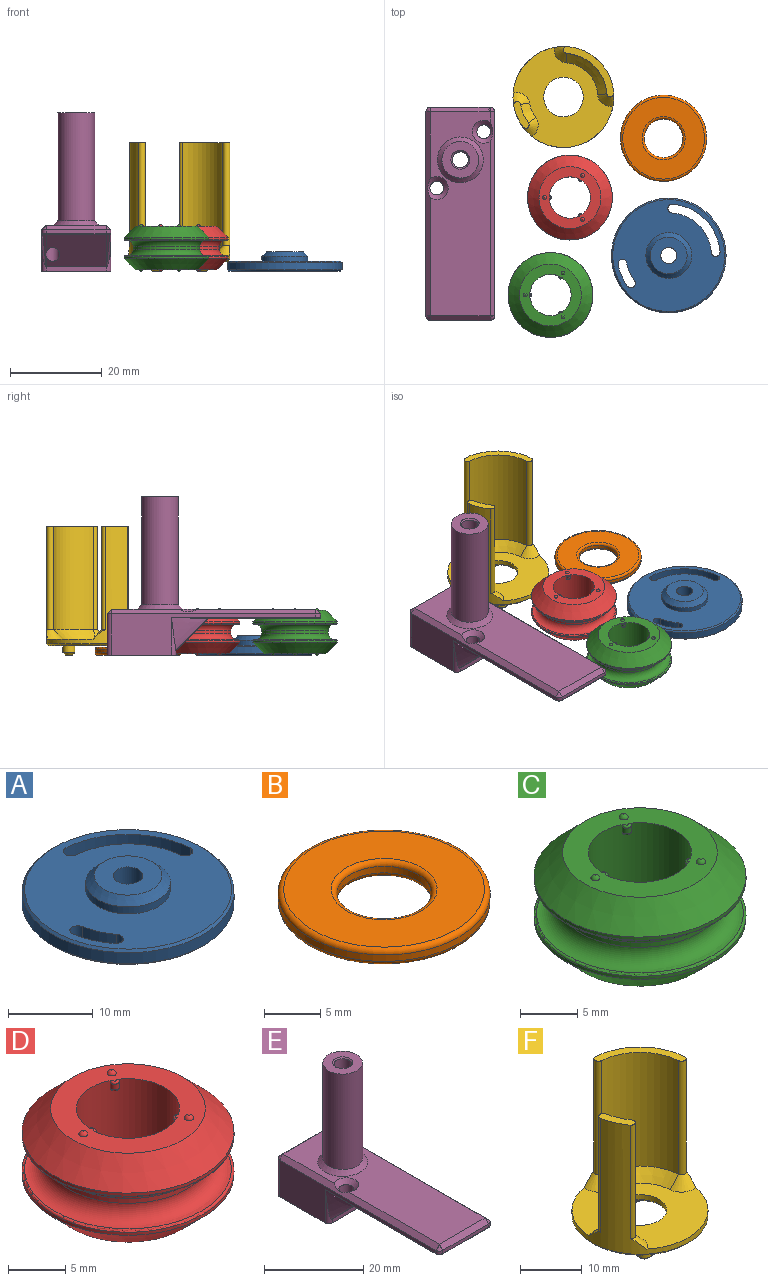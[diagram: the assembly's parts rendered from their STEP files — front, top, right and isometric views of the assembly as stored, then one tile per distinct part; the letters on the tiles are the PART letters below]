
ASSEMBLY  parts=6 mates=5
PART A: 28 faces, bbox 25x25x4.2 mm
  f0: cylinder r=1.75mm len=3.5mm, axis (0,0,1), area 38.5mm2, adj f22,f25
  f1: cylinder r=11.2mm len=4.76mm, axis (0,0,1), area 9.9mm2, adj f2,f7,f11,f16
  f2: cylinder r=0.95mm len=1.9mm, axis (0,0,1), area 5.7mm2, adj f1,f3,f11,f18
  f3: cylinder r=9.3mm len=3.95mm, axis (0,0,1), area 8.2mm2, adj f2,f7,f11,f19
  f4: cylinder r=9.3mm len=8.59mm, axis (0,0,1), area 25.2mm2, adj f5,f8,f11,f12
  f5: cylinder r=0.95mm len=1.9mm, axis (0,0,1), area 5.7mm2, adj f4,f6,f11,f14
  f6: cylinder r=11.2mm len=10.35mm, axis (0,0,1), area 30.3mm2, adj f5,f8,f11,f15
  f7: cylinder r=0.95mm len=1.9mm, axis (0,0,1), area 5.7mm2, adj f1,f3,f11,f17
  f8: cylinder r=0.95mm len=1.9mm, axis (0,0,1), area 5.7mm2, adj f4,f6,f11,f13
  f9: cylinder r=12.5mm len=25mm, axis (0,0,1), area 125.7mm2, adj f20,f21
  f10: plane 24.4x24.4mm, normal (0,0,-1), area 342.8mm2, adj f12,f13,f14,f15,f16,f17,f18,f19
  f11: plane 24.4x24.4mm, normal (0,0,1), area 346.6mm2, adj f1,f2,f3,f4,f5,f6,f7,f8
  f12: cone r=9mm half-angle=45deg, axis (0,0,1), area 5.5mm2, adj f4,f10,f13,f14
  f13: cone r=1.25mm half-angle=45deg, axis (0,0,-1), area 1.5mm2, adj f8,f10,f12,f15
  f14: cone r=1.25mm half-angle=45deg, axis (0,0,-1), area 1.5mm2, adj f5,f10,f12,f15
  f15: cone r=11.5mm half-angle=45deg, axis (0,0,-1), area 6.9mm2, adj f6,f10,f13,f14
  f16: cone r=11.5mm half-angle=45deg, axis (0,0,-1), area 2.2mm2, adj f1,f10,f17,f18
  f17: cone r=1.25mm half-angle=45deg, axis (0,0,-1), area 1.5mm2, adj f7,f10,f16,f19
  f18: cone r=1.25mm half-angle=45deg, axis (0,0,-1), area 1.5mm2, adj f2,f10,f16,f19
  f19: cone r=9mm half-angle=45deg, axis (0,0,1), area 1.8mm2, adj f3,f10,f17,f18
  f20: cone r=12.2mm half-angle=45deg, axis (0,0,-1), area 32.9mm2, adj f9,f11
  f21: cone r=12.5mm half-angle=45deg, axis (0,0,1), area 32.9mm2, adj f9,f10
  f22: plane 8.2x8.2mm, normal (0,0,-1), area 43.2mm2, adj f0,f23
  f23: cylinder r=4.1mm len=8.2mm, axis (0,0,-1), area 5.2mm2, adj f22,f27
  f24: cylinder r=5mm len=10mm, axis (0,0,-1), area 31.4mm2, adj f11,f26
  f25: plane 8x8mm, normal (0,0,1), area 40.6mm2, adj f0,f26
  f26: cone r=4mm half-angle=45deg, axis (0,0,-1), area 40mm2, adj f24,f25
  f27: cone r=4.1mm half-angle=45deg, axis (0,0,-1), area 19.3mm2, adj f10,f23
PART B: 8 faces, bbox 20.3x20.3x1.7 mm
  f0: cylinder r=4.2mm len=8.4mm, axis (0,0,-1), area 18.5mm2, adj f4,f6
  f1: cylinder r=9.4mm len=18.8mm, axis (0,0,-1), area 41.3mm2, adj f5,f7
  f2: plane 17.8x17.8mm, normal (0,0,1), area 179.4mm2, adj f6,f7
  f3: plane 17.8x17.8mm, normal (0,0,-1), area 179.4mm2, adj f4,f5
  f4: torus R=4.7mm, axis (0,0,1), area 21.6mm2, adj f0,f3
  f5: torus R=8.9mm, axis (0,0,1), area 45.5mm2, adj f1,f3
  f6: torus R=4.7mm, axis (0,0,1), area 21.6mm2, adj f0,f2
  f7: torus R=8.9mm, axis (0,0,1), area 45.5mm2, adj f1,f2
PART C: 48 faces, bbox 21.2x21.2x10.1 mm
  f0: cylinder r=4.5mm len=9.5mm, axis (0,0,-1), area 264mm2, adj f2,f6,f8,f9,f10,f11,f12,f13
  f1: cylinder r=9.25mm len=18.5mm, axis (0,0,-1), area 19mm2, adj f3,f46
  f2: plane 13.5x13.5mm, normal (0,0,-1), area 78.2mm2, adj f0,f3,f26,f28,f30,f39,f41,f43
  f3: cone r=8.75mm half-angle=45deg, axis (0,0,1), area 177.7mm2, adj f1,f2
  f4: cylinder r=7.25mm len=14.5mm, axis (0,0,-1), area 22.8mm2, adj f44,f45
  f5: cylinder r=9.25mm len=18.5mm, axis (0,0,-1), area 19mm2, adj f7,f47
  f6: plane 13.5x13.5mm, normal (0,0,1), area 78.2mm2, adj f0,f7,f14,f16,f18,f33,f35,f37
  f7: cone r=6.75mm half-angle=45deg, axis (0,0,-1), area 177.7mm2, adj f5,f6
  f8: plane 0.4x0.2mm, normal (0,0,-1), area 0.1mm2, adj f0,f19
  f9: cylinder r=0.4mm len=0.8mm, axis (0,0,1), area 0.7mm2, adj f0,f18,f19
  f10: plane 0.37x0.3mm, normal (0,0,-1), area 0.1mm2, adj f0,f17
  f11: cylinder r=0.4mm len=0.74mm, axis (0,0,1), area 0.7mm2, adj f0,f16,f17
  f12: plane 0.37x0.3mm, normal (0,0,-1), area 0.1mm2, adj f0,f15
  f13: cylinder r=0.4mm len=0.74mm, axis (0,0,1), area 0.7mm2, adj f0,f14,f15
  f14: torus R=0.2mm, axis (0,0,1), area 0.3mm2, adj f0,f6,f13
  f15: torus R=0.2mm, axis (0,0,1), area 0.3mm2, adj f0,f12,f13
  f16: torus R=0.2mm, axis (0,0,1), area 0.3mm2, adj f0,f6,f11
  f17: torus R=0.2mm, axis (0,0,1), area 0.3mm2, adj f0,f10,f11
  f18: torus R=0.2mm, axis (0,0,1), area 0.3mm2, adj f0,f6,f9
  f19: torus R=0.2mm, axis (0,0,1), area 0.3mm2, adj f0,f8,f9
  f20: plane 0.4x0.2mm, normal (0,0,1), area 0.1mm2, adj f0,f31
  f21: cylinder r=0.4mm len=0.8mm, axis (0,0,-1), area 0.7mm2, adj f0,f30,f31
  f22: plane 0.37x0.3mm, normal (0,0,1), area 0.1mm2, adj f0,f29
  f23: cylinder r=0.4mm len=0.74mm, axis (0,0,-1), area 0.7mm2, adj f0,f28,f29
  f24: plane 0.37x0.3mm, normal (0,0,1), area 0.1mm2, adj f0,f27
  f25: cylinder r=0.4mm len=0.74mm, axis (0,0,-1), area 0.7mm2, adj f0,f26,f27
  f26: torus R=0.2mm, axis (0,0,1), area 0.3mm2, adj f0,f2,f25
  f27: torus R=0.2mm, axis (0,0,-1), area 0.3mm2, adj f0,f24,f25
  f28: torus R=0.2mm, axis (0,0,1), area 0.3mm2, adj f0,f2,f23
  f29: torus R=0.2mm, axis (0,0,-1), area 0.3mm2, adj f0,f22,f23
  f30: torus R=0.2mm, axis (0,0,1), area 0.3mm2, adj f0,f2,f21
  f31: torus R=0.2mm, axis (0,0,-1), area 0.3mm2, adj f0,f20,f21
  f32: plane 0.03x0.03mm, normal (0,0,1), area 0mm2, adj f33
  f33: torus R=0.01mm, axis (0,0,-1), area 0.8mm2, adj f6,f32
  f34: plane 0.03x0.03mm, normal (0,0,1), area 0mm2, adj f35
  f35: torus R=0.01mm, axis (0,0,-1), area 0.8mm2, adj f6,f34
  f36: plane 0.03x0.03mm, normal (0,0,1), area 0mm2, adj f37
  f37: torus R=0.01mm, axis (0,0,-1), area 0.8mm2, adj f6,f36
  f38: plane 0.03x0.03mm, normal (0,0,-1), area 0mm2, adj f39
  f39: torus R=0.01mm, axis (0,0,1), area 0.8mm2, adj f2,f38
  f40: plane 0.03x0.03mm, normal (0,0,-1), area 0mm2, adj f41
  f41: torus R=0.01mm, axis (0,0,1), area 0.8mm2, adj f2,f40
  f42: plane 0.03x0.03mm, normal (0,0,-1), area 0mm2, adj f43
  f43: torus R=0.01mm, axis (0,0,1), area 0.8mm2, adj f2,f42
  f44: torus R=8.75mm, axis (0,0,1), area 130.3mm2, adj f4,f46
  f45: torus R=8.75mm, axis (0,0,1), area 130.3mm2, adj f4,f47
  f46: torus R=9.05mm, axis (0,0,-1), area 20.1mm2, adj f1,f44
  f47: torus R=9.05mm, axis (0,0,-1), area 20.1mm2, adj f5,f45
PART D: 48 faces, bbox 21.2x21.2x10.1 mm
  f0: cylinder r=4.5mm len=9.5mm, axis (0,0,-1), area 264mm2, adj f2,f6,f8,f9,f10,f11,f12,f13
  f1: cylinder r=9.25mm len=18.5mm, axis (0,0,-1), area 19mm2, adj f3,f47
  f2: plane 13.5x13.5mm, normal (0,0,-1), area 78.2mm2, adj f0,f3,f26,f28,f30,f39,f41,f43
  f3: cone r=8.75mm half-angle=45deg, axis (0,0,1), area 177.7mm2, adj f1,f2
  f4: cylinder r=7.25mm len=14.5mm, axis (0,0,-1), area 22.8mm2, adj f44,f45
  f5: cylinder r=9.25mm len=18.5mm, axis (0,0,-1), area 19mm2, adj f7,f46
  f6: plane 13.5x13.5mm, normal (0,0,1), area 78.2mm2, adj f0,f7,f14,f16,f18,f33,f35,f37
  f7: cone r=6.75mm half-angle=45deg, axis (0,0,-1), area 177.7mm2, adj f5,f6
  f8: plane 0.4x0.2mm, normal (0,0,-1), area 0.1mm2, adj f0,f19
  f9: cylinder r=0.4mm len=0.8mm, axis (0,0,1), area 0.7mm2, adj f0,f18,f19
  f10: plane 0.37x0.3mm, normal (0,0,-1), area 0.1mm2, adj f0,f17
  f11: cylinder r=0.4mm len=0.74mm, axis (0,0,1), area 0.7mm2, adj f0,f16,f17
  f12: plane 0.37x0.3mm, normal (0,0,-1), area 0.1mm2, adj f0,f15
  f13: cylinder r=0.4mm len=0.74mm, axis (0,0,1), area 0.7mm2, adj f0,f14,f15
  f14: torus R=0.2mm, axis (0,0,1), area 0.3mm2, adj f0,f6,f13
  f15: torus R=0.2mm, axis (0,0,1), area 0.3mm2, adj f0,f12,f13
  f16: torus R=0.2mm, axis (0,0,1), area 0.3mm2, adj f0,f6,f11
  f17: torus R=0.2mm, axis (0,0,1), area 0.3mm2, adj f0,f10,f11
  f18: torus R=0.2mm, axis (0,0,1), area 0.3mm2, adj f0,f6,f9
  f19: torus R=0.2mm, axis (0,0,1), area 0.3mm2, adj f0,f8,f9
  f20: plane 0.4x0.2mm, normal (0,0,1), area 0.1mm2, adj f0,f31
  f21: cylinder r=0.4mm len=0.8mm, axis (0,0,-1), area 0.7mm2, adj f0,f30,f31
  f22: plane 0.37x0.3mm, normal (0,0,1), area 0.1mm2, adj f0,f29
  f23: cylinder r=0.4mm len=0.74mm, axis (0,0,-1), area 0.7mm2, adj f0,f28,f29
  f24: plane 0.37x0.3mm, normal (0,0,1), area 0.1mm2, adj f0,f27
  f25: cylinder r=0.4mm len=0.74mm, axis (0,0,-1), area 0.7mm2, adj f0,f26,f27
  f26: torus R=0.2mm, axis (0,0,1), area 0.3mm2, adj f0,f2,f25
  f27: torus R=0.2mm, axis (0,0,-1), area 0.3mm2, adj f0,f24,f25
  f28: torus R=0.2mm, axis (0,0,1), area 0.3mm2, adj f0,f2,f23
  f29: torus R=0.2mm, axis (0,0,-1), area 0.3mm2, adj f0,f22,f23
  f30: torus R=0.2mm, axis (0,0,1), area 0.3mm2, adj f0,f2,f21
  f31: torus R=0.2mm, axis (0,0,-1), area 0.3mm2, adj f0,f20,f21
  f32: plane 0.03x0.03mm, normal (0,0,1), area 0mm2, adj f33
  f33: torus R=0.01mm, axis (0,0,-1), area 0.8mm2, adj f6,f32
  f34: plane 0.03x0.03mm, normal (0,0,1), area 0mm2, adj f35
  f35: torus R=0.01mm, axis (0,0,-1), area 0.8mm2, adj f6,f34
  f36: plane 0.03x0.03mm, normal (0,0,1), area 0mm2, adj f37
  f37: torus R=0.01mm, axis (0,0,-1), area 0.8mm2, adj f6,f36
  f38: plane 0.03x0.03mm, normal (0,0,-1), area 0mm2, adj f39
  f39: torus R=0.01mm, axis (0,0,1), area 0.8mm2, adj f2,f38
  f40: plane 0.03x0.03mm, normal (0,0,-1), area 0mm2, adj f41
  f41: torus R=0.01mm, axis (0,0,1), area 0.8mm2, adj f2,f40
  f42: plane 0.03x0.03mm, normal (0,0,-1), area 0mm2, adj f43
  f43: torus R=0.01mm, axis (0,0,1), area 0.8mm2, adj f2,f42
  f44: torus R=8.75mm, axis (0,0,1), area 130.3mm2, adj f4,f47
  f45: torus R=8.75mm, axis (0,0,1), area 130.3mm2, adj f4,f46
  f46: torus R=9.05mm, axis (0,0,-1), area 20.1mm2, adj f5,f45
  f47: torus R=9.05mm, axis (0,0,-1), area 20.1mm2, adj f1,f44
PART E: 41 faces, bbox 16x47.3x35.3 mm
  f0: plane 13x0.8mm, normal (0,-1,0), area 10.4mm2, adj f16,f19,f28,f33
  f1: plane 44.5x9mm, normal (1,0,0), area 142.2mm2, adj f5,f14,f16,f17,f23,f31
  f2: plane 13x9mm, normal (0,1,0), area 117mm2, adj f5,f17,f18,f22
  f3: plane 44.5x9mm, normal (-1,0,0), area 142.2mm2, adj f5,f15,f18,f19,f27,f35
  f4: plane 44.5x13mm, normal (0,0,1), area 467.3mm2, adj f20,f22,f23,f25,f27,f28,f30
  f5: plane 15x15mm, normal (0,0,-1), area 207.5mm2, adj f1,f2,f3,f6,f7,f12,f14,f15
  f6: cylinder r=1.75mm len=34.2mm, axis (0,0,1), area 376mm2, adj f5,f13
  f7: plane 13x1mm, normal (0,-1,0), area 13mm2, adj f5,f14,f15,f38
  f8: plane 24.34x14.6mm, normal (0,0,-1), area 354.5mm2, adj f31,f32,f33,f34,f35,f37,f38,f39
  f9: cylinder r=4mm len=23.5mm, axis (0,0,-1), area 590.6mm2, adj f10,f30
  f10: plane 8x8mm, normal (0,0,1), area 37.1mm2, adj f9,f13
  f11: cylinder r=1.5mm len=6.86mm, axis (0,0,1), area 50.5mm2, adj f25,f37,f38
  f12: cylinder r=1.5mm len=9mm, axis (0,0,1), area 84.8mm2, adj f5,f20
  f13: cone r=1.75mm half-angle=45deg, axis (0,0,1), area 5.1mm2, adj f6,f10
  f14: cylinder r=1mm len=8.2mm, axis (0,0,1), area 5.5mm2, adj f1,f5,f7,f39,f40
  f15: cylinder r=1mm len=8.2mm, axis (0,0,-1), area 5.5mm2, adj f3,f5,f7,f36,f37
  f16: cylinder r=1mm len=1mm, axis (0,0,1), area 1.3mm2, adj f0,f1,f26,f32
  f17: cylinder r=1mm len=9mm, axis (0,0,-1), area 14.1mm2, adj f1,f2,f5,f21
  f18: cylinder r=1mm len=9mm, axis (0,0,1), area 14.1mm2, adj f2,f3,f5,f24
  f19: cylinder r=1mm len=1mm, axis (0,0,-1), area 1.3mm2, adj f0,f3,f29,f34
  f20: cone r=1.5mm half-angle=45deg, axis (0,0,1), area 16mm2, adj f4,f12,f23
  f21: cone r=1mm half-angle=45deg, axis (0,0,-1), area 1.5mm2, adj f17,f22,f23
  f22: plane 13.77x1.77mm, normal (0,0.71,0.71), area 18.4mm2, adj f2,f4,f21,f24
  f23: plane 44.94x1.44mm, normal (0.71,0,0.71), area 60.7mm2, adj f1,f4,f20,f21,f26
  f24: cone r=1mm half-angle=45deg, axis (0,0,-1), area 0.7mm2, adj f18,f22,f27
  f25: cone r=1.5mm half-angle=45deg, axis (0,0,1), area 15.3mm2, adj f4,f11,f27
  f26: cone r=1mm half-angle=45deg, axis (0,0,-1), area 1.1mm2, adj f16,f23,f28
  f27: plane 44.5x1mm, normal (-0.71,0,0.71), area 60.7mm2, adj f3,f4,f24,f25,f29
  f28: plane 13x1mm, normal (0,-0.71,0.71), area 18.4mm2, adj f0,f4,f26,f29
  f29: cone r=1mm half-angle=45deg, axis (0,0,-1), area 1.1mm2, adj f19,f27,f28
  f30: cone r=4mm half-angle=45deg, axis (0,0,-1), area 40mm2, adj f4,f9
  f31: cylinder r=0.2mm len=31.5mm, axis (0,-1,0), area 8.4mm2, adj f1,f8,f32,f40
  f32: torus R=0.8mm, axis (0,0,-1), area 0.5mm2, adj f8,f16,f31,f33
  f33: cylinder r=0.2mm len=13mm, axis (-1,0,0), area 4.1mm2, adj f0,f8,f32,f34
  f34: torus R=0.8mm, axis (0,0,-1), area 0.5mm2, adj f8,f19,f33,f35
  f35: cylinder r=0.2mm len=31.5mm, axis (0,1,0), area 8.4mm2, adj f3,f8,f34,f36
  f36: bspline ~7.96x7.2mm, area 16.6mm2, adj f15,f35,f37
  f37: cone r=8mm half-angle=45deg, axis (0,0,1), area 4.3mm2, adj f8,f11,f15,f36,f38
  f38: plane 13x7mm, normal (0,-0.71,-0.71), area 118.8mm2, adj f7,f8,f11,f37,f39
  f39: cone r=8mm half-angle=45deg, axis (0,0,1), area 4.5mm2, adj f8,f14,f38,f40
  f40: bspline ~7.96x7.2mm, area 16.6mm2, adj f14,f31,f39
PART F: 26 faces, bbox 25.8x24x28 mm
  f0: plane 5.86x3.37mm, normal (0,0,1), area 8.9mm2, adj f1,f4,f9,f11
  f1: cylinder r=9.5mm len=22.5mm, axis (0,0,-1), area 99.8mm2, adj f0,f9,f11,f24
  f2: plane 10.97x10.97mm, normal (0,0,1), area 23.7mm2, adj f4,f6,f8,f10
  f3: cylinder r=4.3mm len=8.6mm, axis (0,0,-1), area 27mm2, adj f7,f16
  f4: cylinder r=11mm len=25.5mm, axis (0,0,-1), area 589.8mm2, adj f0,f2,f7,f8,f9,f10,f11,f19
  f5: plane 21x21mm, normal (0,0,-1), area 263.4mm2, adj f12,f14,f16,f19
  f6: cylinder r=9.5mm len=22.5mm, axis (0,0,-1), area 304.4mm2, adj f2,f8,f10,f21
  f7: plane 21.83x21.8mm, normal (0,0,1), area 230.1mm2, adj f3,f4,f20,f21,f22,f23,f24,f25
  f8: cylinder r=0.75mm len=22.5mm, axis (0,0,-1), area 53mm2, adj f2,f4,f6,f20
  f9: cylinder r=0.75mm len=22.5mm, axis (0,0,-1), area 53mm2, adj f0,f1,f4,f25
  f10: cylinder r=0.75mm len=22.5mm, axis (0,0,-1), area 53mm2, adj f2,f4,f6,f22
  f11: cylinder r=0.75mm len=22.5mm, axis (0,0,-1), area 53mm2, adj f0,f1,f4,f23
  f12: cylinder r=1.3mm len=2.6mm, axis (0,0,1), area 12.3mm2, adj f5,f18
  f13: plane 1.6x1.6mm, normal (0,0,-1), area 2mm2, adj f18
  f14: cylinder r=1.3mm len=2.6mm, axis (0,0,1), area 12.3mm2, adj f5,f17
  f15: plane 1.6x1.6mm, normal (0,0,-1), area 2mm2, adj f17
  f16: cone r=4.8mm half-angle=45deg, axis (0,0,-1), area 20.2mm2, adj f3,f5
  f17: cone r=1.3mm half-angle=45deg, axis (0,0,1), area 4.7mm2, adj f14,f15
  f18: cone r=1.3mm half-angle=45deg, axis (0,0,1), area 4.7mm2, adj f12,f13
  f19: cone r=11mm half-angle=45deg, axis (0,0,1), area 47.8mm2, adj f4,f5
  f20: cone r=2.75mm half-angle=45deg, axis (0,0,-1), area 9.6mm2, adj f4,f7,f8,f21
  f21: cone r=7.5mm half-angle=45deg, axis (0,0,1), area 34.2mm2, adj f6,f7,f20,f22
  f22: cone r=2.75mm half-angle=45deg, axis (0,0,-1), area 9.6mm2, adj f4,f7,f10,f21
  f23: cone r=2.75mm half-angle=45deg, axis (0,0,-1), area 9.6mm2, adj f4,f7,f11,f24
  f24: cone r=7.5mm half-angle=45deg, axis (0,0,1), area 11.2mm2, adj f1,f7,f23,f25
  f25: cone r=2.75mm half-angle=45deg, axis (0,0,-1), area 9.6mm2, adj f4,f7,f9,f24
PLACE A t=(16.73,-0.03,-50.66)mm
PLACE B t=(15.6,25.53,-38.66)mm
PLACE C t=(-9.05,-8.64,-40.46)mm
PLACE D t=(-4.81,12.6,-28.46)mm
PLACE E t=(-28.7,20.79,-16.86)mm
PLACE F t=(-6.22,34.5,-24.86)mm
MATE planar A.f10 <-> B.f1  axis (0,0,-1) through (16.4,0.37,-16.86)mm
MATE planar F.f12 <-> D.f33  axis (0,0,-1) through (-1.1,41.65,-16.86)mm
MATE planar F.f14 <-> E.f18  axis (0,0,-1) through (-11.35,29.36,-16.86)mm
MATE planar B.f1 <-> C.f35  axis (0,0,-1) through (15.6,26.53,-16.86)mm
MATE planar D.f37 <-> B.f1  axis (0,0,1) through (-2.06,18.36,-16.86)mm
